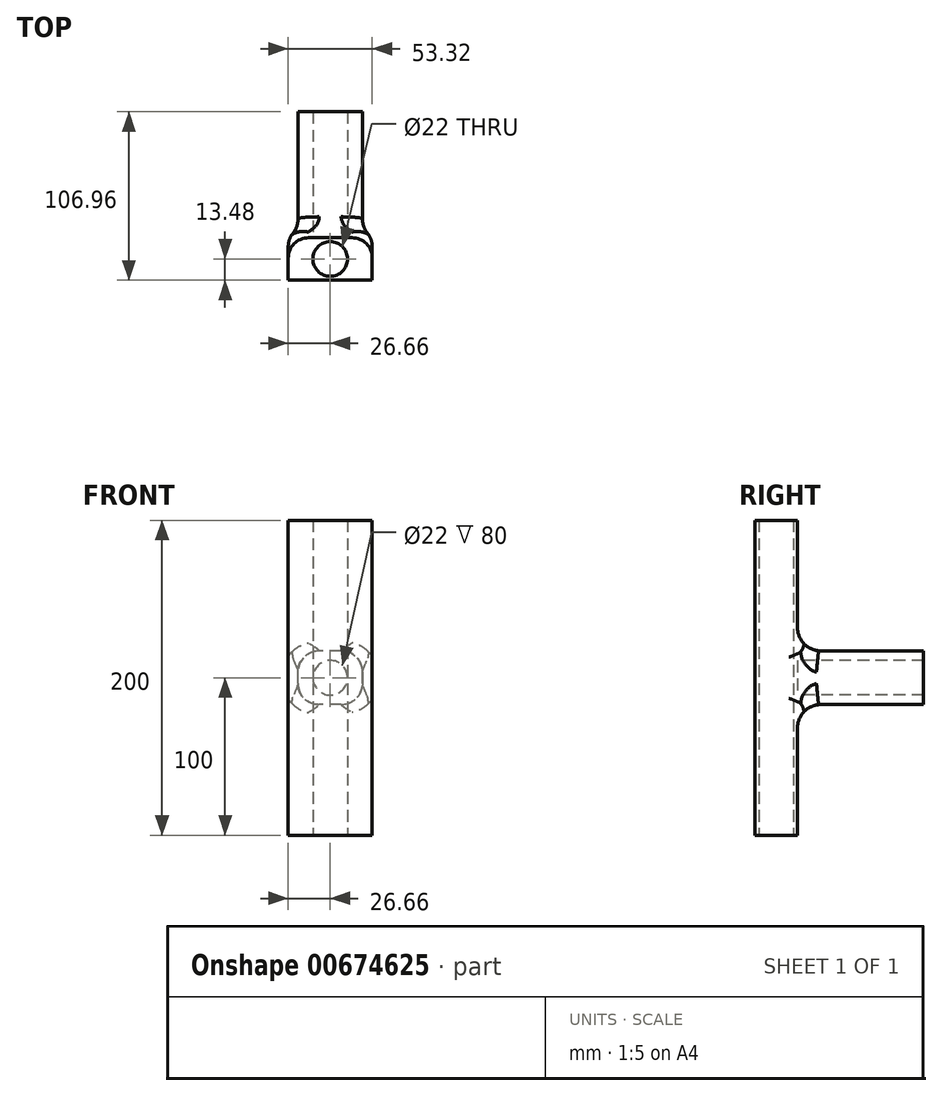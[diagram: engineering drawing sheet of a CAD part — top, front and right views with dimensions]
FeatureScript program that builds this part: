
annotation { "Feature Type Name" : "Feature", "Feature Type Description" : "" }
export const myFeature = defineFeature(function(context is Context, id is Id, definition is map)
    precondition{}
    {
        {
            var Q0;
            Q0=qCreatedBy(makeId("Top.planeOp"),FACE);
            var sketch = newSketch(context, id + "F0", { "sketchPlane" : qUnion([Q0])});
            skCircle(sketch, "E0", {"center": v(0, 0) * mm, "radius": 11 * mm});
            skLineSegment(sketch, "E1.bottom", {"start": v(26.66, 13.48) * mm, "end": v(-26.66, 13.48) * mm});
            skLineSegment(sketch, "E1.top", {"start": v(26.66, -13.48) * mm, "end": v(-26.66, -13.48) * mm});
            skLineSegment(sketch, "E1.left", {"start": v(26.66, 13.48) * mm, "end": v(26.66, -13.48) * mm});
            skLineSegment(sketch, "E1.right", {"start": v(-26.66, 13.48) * mm, "end": v(-26.66, -13.48) * mm});
            skSolve(sketch);
        }
        {
            var Q0;
            Q0=makeQuery(id+"F0.imprint","IMPRINT",FACE,{"disambiguationData":[TD([[makeQuery(id+"F0.imprint","IMPRINT",EDGE,{"derivedFrom":sQuery(id+"F0.wireOp",EDGE,"E0")}),-1.0]])]});
            extrude(context, id + "F1", {"entities" : qUnion([Q0]), "endBound" : BoundingType.SYMMETRIC, "depth" : 200 * mm, "offsetDistance" : 25 * mm});
        }
        {
            var Q0;
            Q0=makeQuery(id+"F1.opExtrude","SWEPT_FACE",FACE,{"disambiguationData":[OSD([sQuery(id+"F0.wireOp",EDGE,"E1.bottom")])]});
            var sketch = newSketch(context, id + "F2", { "sketchPlane" : qUnion([Q0])});
            skCircle(sketch, "E2", {"center": v(0, 0) * mm, "radius": 11 * mm});
            skLineSegment(sketch, "E3.bottom", {"start": v(-20.47, -17.07) * mm, "end": v(20.47, -17.07) * mm});
            skLineSegment(sketch, "E3.top", {"start": v(-20.47, 17.07) * mm, "end": v(20.47, 17.07) * mm});
            skLineSegment(sketch, "E3.left", {"start": v(-20.47, -17.07) * mm, "end": v(-20.47, 17.07) * mm});
            skLineSegment(sketch, "E3.right", {"start": v(20.47, -17.07) * mm, "end": v(20.47, 17.07) * mm});
            skSolve(sketch);
        }
        {
            var Q0;
            Q0=qSketchRegion(id+"F2",true);
            extrude(context, id + "F3", {"entities" : qUnion([Q0]), "operationType" : NewBodyOperationType.ADD, "depth" : 80 * mm, "offsetDistance" : 25 * mm});
        }
        {
            var Q0;
            Q0=makeQuery(id+"F3.opExtrude","CAP_EDGE",EDGE,{"disambiguationData":[OSD([sQuery(id+"F2.wireOp",EDGE,"E3.top")])],"isStart":true});
            var Q1;
            Q1=makeQuery(id+"F3.opExtrude","CAP_EDGE",EDGE,{"disambiguationData":[OSD([sQuery(id+"F2.wireOp",EDGE,"E3.bottom")])],"isStart":true});
            var Q2;
            Q2=makeQuery(id+"F3.opExtrude","CAP_EDGE",EDGE,{"disambiguationData":[OSD([sQuery(id+"F2.wireOp",EDGE,"E3.right")])],"isStart":true});
            var Q3;
            Q3=makeQuery(id+"F3.opExtrude","CAP_EDGE",EDGE,{"disambiguationData":[OSD([sQuery(id+"F2.wireOp",EDGE,"E3.left")])],"isStart":true});
            fillet(context, id + "F4", {"entities" : qUnion([Q0, Q1, Q2, Q3]), "radius" : 14.73 * mm, "tangentPropagation" : true, "allowEdgeOverflow" : false});
        }
        {
            var Q0;
            Q0=makeQuery(id+"F1.opExtrude","SWEPT_EDGE",EDGE,{"disambiguationData":[OSD([sQuery(id+"F0.wireOp",EDGE,"E1.bottom"),sQuery(id+"F0.wireOp",EDGE,"E1.left")])]});
            var Q1;
            Q1=makeQuery(id+"F4.opFillet","BLEND_EDGE",EDGE,{"blendedFrom":[makeQuery(id+"F3.opExtrude","CAP_EDGE",EDGE,{"disambiguationData":[OSD([sQuery(id+"F2.wireOp",EDGE,"E3.left")])],"isStart":true}),makeQuery(id+"F1.opExtrude","SWEPT_FACE",FACE,{"disambiguationData":[OSD([sQuery(id+"F0.wireOp",EDGE,"E1.left")])]})],"blendedInto":[makeQuery(id+"F1.opExtrude","SWEPT_FACE",FACE,{"disambiguationData":[OSD([sQuery(id+"F0.wireOp",EDGE,"E1.left")])]})]});
            var Q2;
            Q2=makeQuery(id+"F1.opExtrude","SWEPT_EDGE",EDGE,{"disambiguationData":[OSD([sQuery(id+"F0.wireOp",EDGE,"E1.bottom"),sQuery(id+"F0.wireOp",EDGE,"E1.left")])]});
            var Q3;
            Q3=makeQuery(id+"F1.opExtrude","SWEPT_EDGE",EDGE,{"disambiguationData":[OSD([sQuery(id+"F0.wireOp",EDGE,"E1.bottom"),sQuery(id+"F0.wireOp",EDGE,"E1.right")])]});
            var Q4;
            Q4=makeQuery(id+"F4.opFillet","BLEND_EDGE",EDGE,{"blendedFrom":[makeQuery(id+"F3.opExtrude","CAP_EDGE",EDGE,{"disambiguationData":[OSD([sQuery(id+"F2.wireOp",EDGE,"E3.right")])],"isStart":true}),makeQuery(id+"F1.opExtrude","SWEPT_FACE",FACE,{"disambiguationData":[OSD([sQuery(id+"F0.wireOp",EDGE,"E1.right")])]})],"blendedInto":[makeQuery(id+"F1.opExtrude","SWEPT_FACE",FACE,{"disambiguationData":[OSD([sQuery(id+"F0.wireOp",EDGE,"E1.right")])]})]});
            var Q5;
            Q5=makeQuery(id+"F1.opExtrude","SWEPT_EDGE",EDGE,{"disambiguationData":[OSD([sQuery(id+"F0.wireOp",EDGE,"E1.bottom"),sQuery(id+"F0.wireOp",EDGE,"E1.right")])]});
            fillet(context, id + "F5", {"entities" : qUnion([Q0, Q1, Q2, Q3, Q4, Q5]), "radius" : 12.77 * mm, "tangentPropagation" : true, "allowEdgeOverflow" : false});
        }
        {
            var Q0;
            Q0=makeQuery(id+"F3.opExtrude","SWEPT_EDGE",EDGE,{"disambiguationData":[OSD([sQuery(id+"F2.wireOp",EDGE,"E3.top"),sQuery(id+"F2.wireOp",EDGE,"E3.left")])]});
            var Q1;
            Q1=makeQuery(id+"F3.opExtrude","SWEPT_EDGE",EDGE,{"disambiguationData":[OSD([sQuery(id+"F2.wireOp",EDGE,"E3.top"),sQuery(id+"F2.wireOp",EDGE,"E3.right")])]});
            var Q2;
            Q2=makeQuery(id+"F3.opExtrude","SWEPT_EDGE",EDGE,{"disambiguationData":[OSD([sQuery(id+"F2.wireOp",EDGE,"E3.bottom"),sQuery(id+"F2.wireOp",EDGE,"E3.right")])]});
            var Q3;
            Q3=makeQuery(id+"F3.opExtrude","SWEPT_EDGE",EDGE,{"disambiguationData":[OSD([sQuery(id+"F2.wireOp",EDGE,"E3.bottom"),sQuery(id+"F2.wireOp",EDGE,"E3.left")])]});
            fillet(context, id + "F6", {"entities" : qUnion([Q0, Q1, Q2, Q3]), "radius" : 13.52 * mm, "tangentPropagation" : true, "allowEdgeOverflow" : false});
        }
    });
